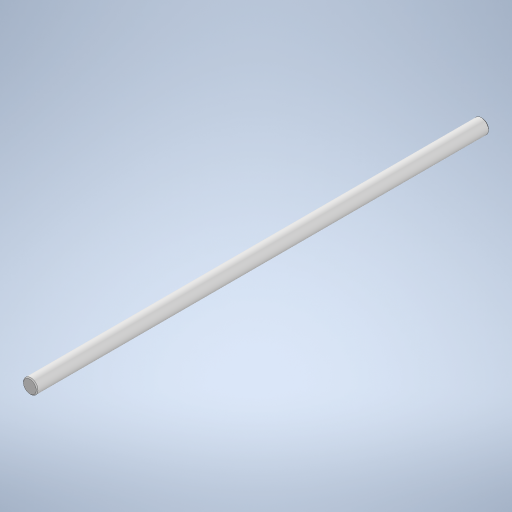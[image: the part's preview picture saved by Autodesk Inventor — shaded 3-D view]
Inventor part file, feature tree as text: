
AUTODESK INVENTOR PART (.ipt)
format: ipt  version: 2024 (Build 280153000, 153)  size: 240,128 bytes
history: native  units: mm
features: extrude x1, chamfer x1, sketch x1
ambient origin geometry x8: Origin, YZ Plane, XZ Plane, XY Plane, X Axis, Y Axis, Z Axis, Center Point
bodies: Solid1 (feature_tree)
feature tree (3):
  extrude  "Extrusion1"  Depth=250.0mm TaperAngle=0.0deg
  chamfer  "Chamfer1"  Distance=0.5mm Angle=45.0deg
  sketch  "Sketch1"  dims[d0=8.0mm d1=250.0mm d2=0.0mm d3=0.5mm d4=2.0mm d5=45.0deg]
